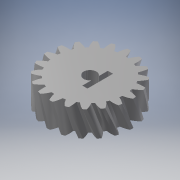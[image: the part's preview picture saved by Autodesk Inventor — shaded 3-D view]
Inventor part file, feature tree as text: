
AUTODESK INVENTOR PART (.ipt)
format: ipt  version: 2017 SP1 (Build 210196100, 196)  size: 906,752 bytes
history: native  units: mm (DEFAULTED — no unit token found)
features: plane x3, other x3, sketch x3, extrude x2
ambient origin geometry x8: Origin, YZ Plane, XZ Plane, XY Plane, X Axis, Y Axis, Z Axis, Center Point
bodies: Solid1 (feature_tree)
feature tree (11):
  extrude  "Extrusion1"  Depth=10.0mm TaperAngle=0.0deg
  plane  "Work Plane2"
  plane  "Work Plane8"
  plane  "Work Plane9"
  other  "Engrenage cylindrique"
  extrude  "Extrusion2"  Depth=10.0mm TaperAngle=0.0deg
  sketch  "Sketch1"  dims[d0=32.749068mm d1=10.0mm d2=0.0mm]
  sketch  "Sketch2"  dims[d3=30.066593mm d4=10.0mm d5=0.0mm d16=30.066593mm d17=0.0mm d34=1.570796mm d39=0.0mm d41=0.0mm d43=30.066593mm d46=30.066593mm d47=0.0mm d48=0.0mm d49=5.0mm d50=5.0mm d51=5.0mm d52=2.0mm d53=2.0mm d54=10.0mm d55=0.0mm]
  other  "Srf1"
  sketch  "Esquisse3"
  other  "Diamètre primitif"
